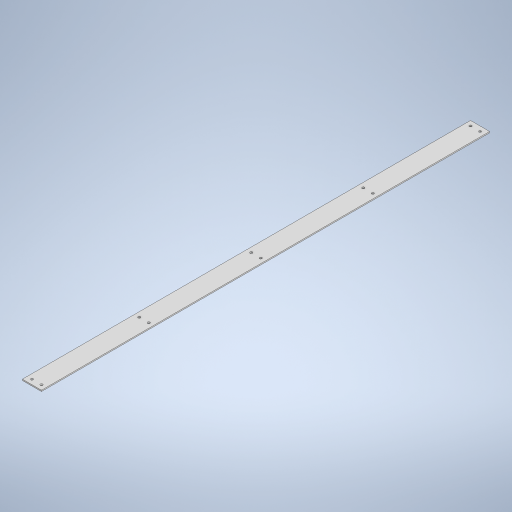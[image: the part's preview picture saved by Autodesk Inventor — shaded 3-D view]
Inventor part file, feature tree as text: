
AUTODESK INVENTOR PART (.ipt)
format: ipt  version: 2023 (Build 270158030, 158C)  size: 262,656 bytes
history: native  units: in
note: dims shown in document units (in); Inventor stores cm internally (conversion verified against a paired STEP export)
features: extrude x1, sketch x1
ambient origin geometry x8: Origin, YZ Plane, XZ Plane, XY Plane, X Axis, Y Axis, Z Axis, Center Point
bodies: Solid1 (feature_tree)
feature tree (2):
  extrude  "Extrusion1"  Depth=47.0in
  sketch  "Sketch1"  dims[d0=2.0in d1=47.0in d2=0.125in d3=0.0in d4=0.25in d5=0.5in d6=0.5in d7=0.25in d8=11.75in d9=0.25in d10=23.5in d11=0.25in]
